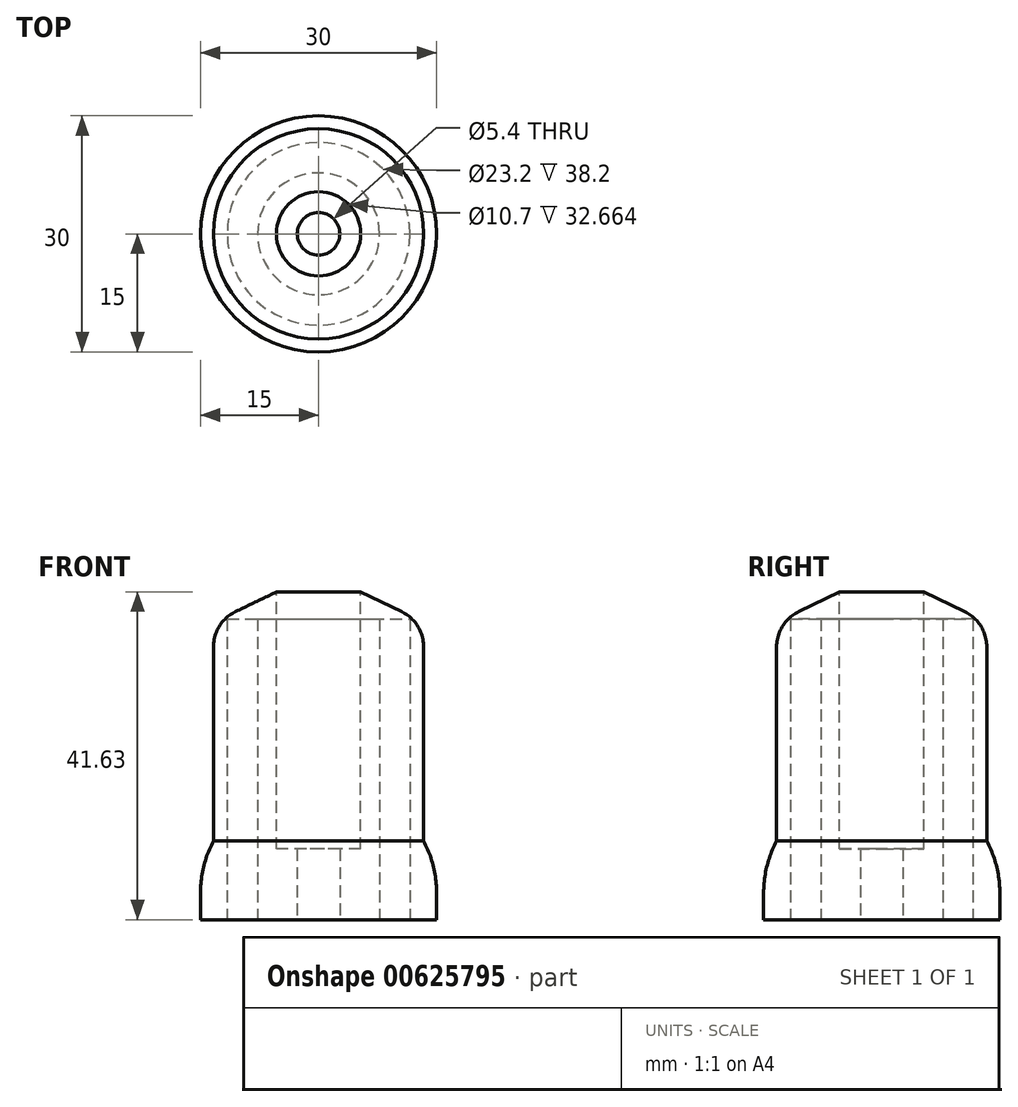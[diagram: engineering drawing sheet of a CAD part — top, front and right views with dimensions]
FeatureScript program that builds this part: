
annotation { "Feature Type Name" : "Feature", "Feature Type Description" : "" }
export const myFeature = defineFeature(function(context is Context, id is Id, definition is map)
    precondition{}
    {
        {
            var Q0;
            Q0=qCreatedBy(makeId("Front.planeOp"),FACE);
            var sketch = newSketch(context, id + "F0", { "sketchPlane" : qUnion([Q0])});
            skLineSegment(sketch, "E0", {"start": v(0, 18.93) * mm, "end": v(0, -25.27) * mm});
            skLineSegment(sketch, "E1", {"start": v(0, -25.27) * mm, "end": v(-15, -25.27) * mm});
            skLineSegment(sketch, "E2", {"start": v(-15, -25.27) * mm, "end": v(-15, -15.27) * mm});
            skLineSegment(sketch, "E3", {"start": v(-15, -15.27) * mm, "end": v(-13.35, -15.27) * mm});
            skLineSegment(sketch, "E4", {"start": v(-13.35, -15.27) * mm, "end": v(-13.35, 12.53) * mm});
            skLineSegment(sketch, "E5", {"start": v(0, 18.93) * mm, "end": v(-13.35, 12.53) * mm});
            skSolve(sketch);
        }
        {
            var Q0;
            Q0=makeQuery(id+"F0.imprint","IMPRINT",FACE,{"disambiguationData":[TD([[makeQuery(id+"F0.imprint","IMPRINT",EDGE,{"derivedFrom":sQuery(id+"F0.wireOp",EDGE,"E0")}),-1.0]])]});
            var Q1;
            Q1=sQuery(id+"F0.wireOp",EDGE,"E0");
            revolve(context, id + "F1", {"surfaceOperationType" : NewSurfaceOperationType.NEW, "entities" : qUnion([Q0]), "axis" : qUnion([Q1]), "revolveType" : RevolveType.FULL});
        }
        {
            var Q0;
            Q0=makeQuery(id+"F1.opRevolve","SWEPT_FACE",FACE,{"disambiguationData":[OSD([sQuery(id+"F0.wireOp",EDGE,"E1")])]});
            var sketch = newSketch(context, id + "F2", { "sketchPlane" : qUnion([Q0])});
            skCircle(sketch, "E6", {"center": v(0, 0) * mm, "radius": 2.7 * mm});
            skSolve(sketch);
        }
        {
            var Q0;
            Q0 = qSketchRegion(id + "F2", true);
            extrude(context, id + "F3", {"entities" : qUnion([Q0]), "operationType" : NewBodyOperationType.REMOVE, "endBound" : BoundingType.THROUGH_ALL, "oppositeDirection" : true, "depth" : 25 * mm, "offsetDistance" : 25 * mm});
        }
        {
            var Q0;
            Q0=makeQuery(id+"F1.opRevolve","SWEPT_FACE",FACE,{"disambiguationData":[OSD([sQuery(id+"F0.wireOp",EDGE,"E1")])]});
            var sketch = newSketch(context, id + "F4", { "sketchPlane" : qUnion([Q0])});
            skCircle(sketch, "E7", {"center": v(0, 0) * mm, "radius": 7.75 * mm});
            skCircle(sketch, "E8", {"center": v(0, 0) * mm, "radius": 11.6 * mm});
            skSolve(sketch);
        }
        {
            var Q0;
            Q0 = qSketchRegion(id + "F4", true);
            extrude(context, id + "F5", {"entities" : qUnion([Q0]), "operationType" : NewBodyOperationType.REMOVE, "oppositeDirection" : true, "depth" : 38.2 * mm, "offsetDistance" : 25 * mm});
        }
        {
            var Q0;
            Q0=makeQuery(id+"F1.opRevolve","SWEPT_EDGE",EDGE,{"disambiguationData":[OSD([sQuery(id+"F0.wireOp",EDGE,"E4"),sQuery(id+"F0.wireOp",EDGE,"E5")])]});
            fillet(context, id + "F6", {"entities" : qUnion([Q0]), "radius" : 5 * mm, "tangentPropagation" : true, "allowEdgeOverflow" : false});
        }
        {
            var Q0;
            Q0=qCreatedBy(makeId("Top.planeOp"),FACE);
            cPlane(context, id + "F7", {"entities" : qUnion([Q0]), "cplaneType" : CPlaneType.OFFSET, "offset" : 17.8 * mm, "width" : 150 * mm, "height" : 150 * mm});
        }
        {
            var Q0;
            Q0=qCreatedBy(id+"F7.planeOp",FACE);
            var sketch = newSketch(context, id + "F8", { "sketchPlane" : qUnion([Q0])});
            skCircle(sketch, "E9.0", {"center": v(0, 0) * mm, "radius": 5.35 * mm});
            skSolve(sketch);
        }
        {
            var Q0;
            Q0 = qSketchRegion(id + "F8", true);
            extrude(context, id + "F9", {"entities" : qUnion([Q0]), "operationType" : NewBodyOperationType.REMOVE, "oppositeDirection" : true, "depth" : 34.1 * mm, "offsetDistance" : 25 * mm});
        }
        {
            var Q0;
            Q0=makeQuery(id+"F1.opRevolve","SWEPT_EDGE",EDGE,{"disambiguationData":[OSD([sQuery(id+"F0.wireOp",EDGE,"E2"),sQuery(id+"F0.wireOp",EDGE,"E3")])]});
            fillet(context, id + "F10", {"entities" : qUnion([Q0]), "radius" : 14 * mm, "tangentPropagation" : true, "allowEdgeOverflow" : false});
        }
    });
